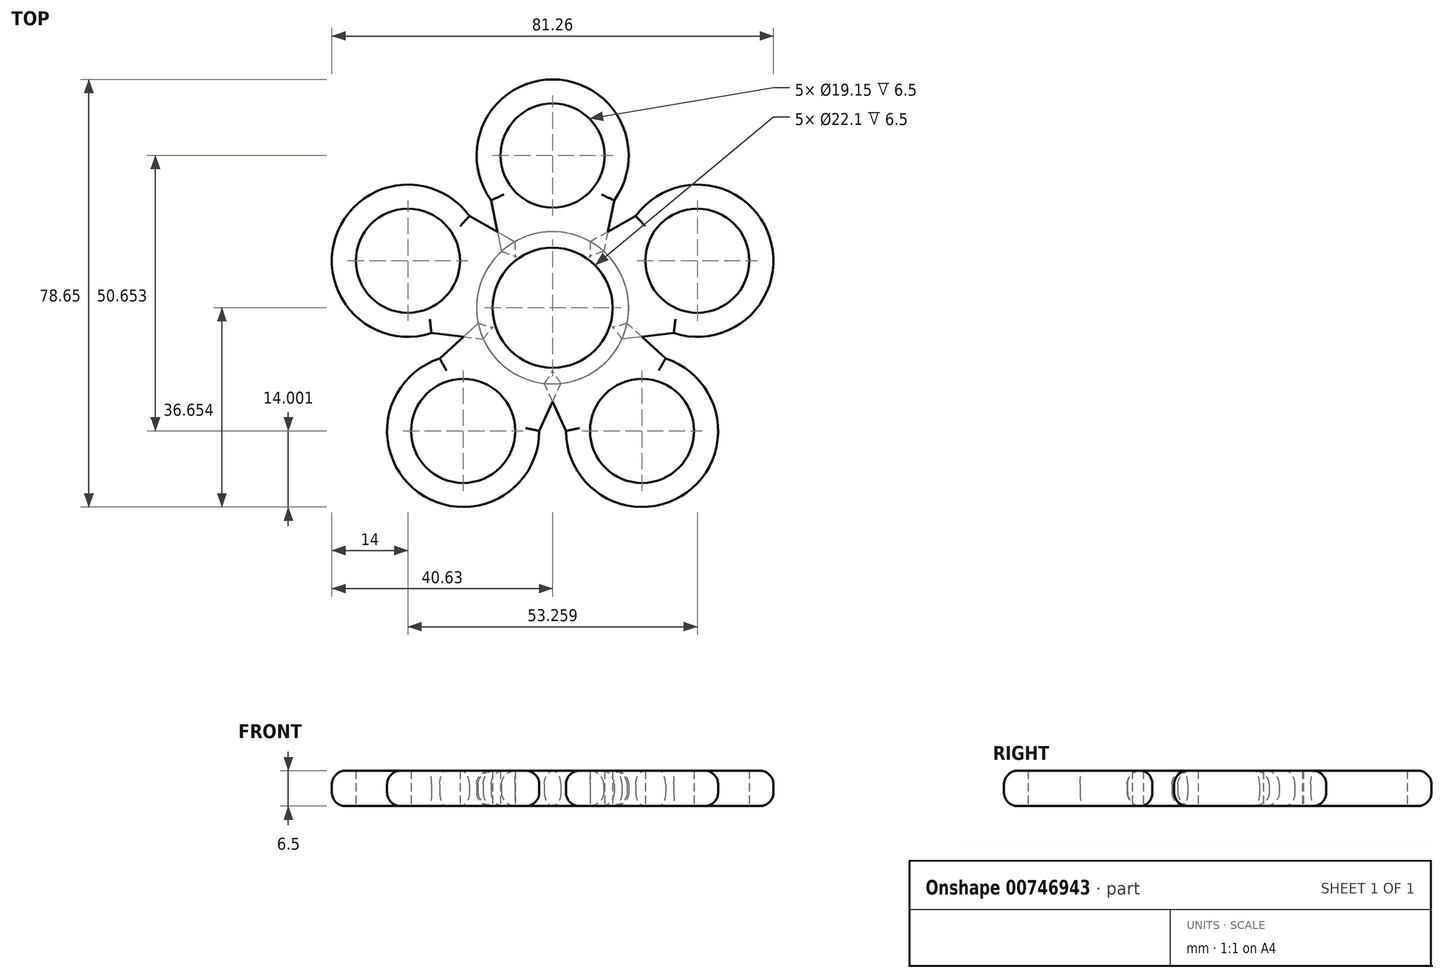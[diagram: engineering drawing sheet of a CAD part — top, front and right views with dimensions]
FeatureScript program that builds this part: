
annotation { "Feature Type Name" : "Feature", "Feature Type Description" : "" }
export const myFeature = defineFeature(function(context is Context, id is Id, definition is map)
    precondition{}
    {
        {
            var Q0;
            Q0=qCreatedBy(makeId("Top.planeOp"),FACE);
            var sketch = newSketch(context, id + "F0", { "sketchPlane" : qUnion([Q0])});
            skLineSegment(sketch, "E0.bottom", {"start": v(3.29, -10.32) * mm, "end": v(-3.29, -10.32) * mm});
            skLineSegment(sketch, "E0.top", {"start": v(13, 17.68) * mm, "end": v(-13, 17.68) * mm});
            skCircle(sketch, "E1", {"center": v(0, 17.68) * mm, "radius": 14 * mm});
            skCircle(sketch, "E2", {"center": v(0, 17.68) * mm, "radius": 9.57 * mm});
            skCircle(sketch, "E3", {"center": v(0, -10.32) * mm, "radius": 14 * mm});
            skCircle(sketch, "E4", {"center": v(0, -10.32) * mm, "radius": 11.05 * mm});
            skLineSegment(sketch, "E5", {"start": v(13, 17.68) * mm, "end": v(9.42, 0.04) * mm});
            skLineSegment(sketch, "E6", {"start": v(-13, 17.68) * mm, "end": v(-9.42, 0.04) * mm});
            skSolve(sketch);
        }
        {
            var Q0;
            {var subQ1=sQuery(id+"F0.wireOp",EDGE,"E0.top");var subQ8=sQuery(id+"F0.wireOp",EDGE,"E5");var subQ10=makeQuery(id+"F0.imprint","INTERSECT",VERTEX,{"derivedFrom":[subQ1,subQ8]});Q0=makeQuery(id+"F0.imprint","IMPRINT",FACE,{"disambiguationData":[TD([[makeQuery(id+"F0.imprint","IMPRINT",EDGE,{"disambiguationData":[TD([[subQ10,-1.0]])],"derivedFrom":subQ1}),-1.0]])]});}
            var Q1;
            {var subQ0=sQuery(id+"F0.wireOp",EDGE,"E5");var subQ6=sQuery(id+"F0.wireOp",EDGE,"E0.top");var subQ10=makeQuery(id+"F0.imprint","INTERSECT",VERTEX,{"derivedFrom":[subQ6,subQ0]});Q1=makeQuery(id+"F0.imprint","IMPRINT",FACE,{"disambiguationData":[TD([[makeQuery(id+"F0.imprint","IMPRINT",EDGE,{"disambiguationData":[TD([[subQ10,-1.0]])],"derivedFrom":subQ6}),1.0]])]});}
            var Q2;
            {var subQ0=sQuery(id+"F0.wireOp",EDGE,"E6");var subQ1=sQuery(id+"F0.wireOp",EDGE,"E1");var subQ2=makeQuery(id+"F0.imprint","INTERSECT",VERTEX,{"derivedFrom":[subQ1,subQ0]});Q2=makeQuery(id+"F0.imprint","IMPRINT",FACE,{"disambiguationData":[TD([[makeQuery(id+"F0.imprint","IMPRINT",EDGE,{"disambiguationData":[TD([[subQ2,-1.0]])],"derivedFrom":subQ1}),-1.0]])]});}
            var Q3;
            Q3=makeQuery(id+"F0.imprint","IMPRINT",FACE,{"disambiguationData":[TD([[makeQuery(id+"F0.imprint","IMPRINT",EDGE,{"derivedFrom":sQuery(id+"F0.wireOp",EDGE,"E4")}),-1.0]])]});
            var Q4;
            {var subQ0=sQuery(id+"F0.wireOp",EDGE,"E5");var subQ1=sQuery(id+"F0.wireOp",EDGE,"E1");var subQ2=makeQuery(id+"F0.imprint","INTERSECT",VERTEX,{"derivedFrom":[subQ1,subQ0]});Q4=makeQuery(id+"F0.imprint","IMPRINT",FACE,{"disambiguationData":[TD([[makeQuery(id+"F0.imprint","IMPRINT",EDGE,{"disambiguationData":[TD([[subQ2,1.0]])],"derivedFrom":subQ1}),-1.0]])]});}
            extrude(context, id + "F1", {"entities" : qUnion([Q0, Q1, Q2, Q3, Q4]), "depth" : 6.5 * mm, "offsetDistance" : 25 * mm});
        }
        {
            var Q0;
            Q0=makeQuery(id+"F1.opExtrude","CAP_EDGE",EDGE,{"disambiguationData":[OSD([sQuery(id+"F0.wireOp",EDGE,"E5")])],"isStart":false});
            var Q1;
            Q1=makeQuery(id+"F1.opExtrude","CAP_EDGE",EDGE,{"disambiguationData":[OSD([sQuery(id+"F0.wireOp",EDGE,"E1")])],"isStart":false});
            var Q2;
            Q2=makeQuery(id+"F1.opExtrude","CAP_EDGE",EDGE,{"disambiguationData":[OSD([sQuery(id+"F0.wireOp",EDGE,"E6")])],"isStart":false});
            var Q3;
            Q3=makeQuery(id+"F1.opExtrude","CAP_EDGE",EDGE,{"disambiguationData":[OSD([sQuery(id+"F0.wireOp",EDGE,"E3")])],"isStart":false});
            var Q4;
            Q4=makeQuery(id+"F1.opExtrude","CAP_EDGE",EDGE,{"disambiguationData":[OSD([sQuery(id+"F0.wireOp",EDGE,"E5")])],"isStart":true});
            var Q5;
            Q5=makeQuery(id+"F1.opExtrude","CAP_EDGE",EDGE,{"disambiguationData":[OSD([sQuery(id+"F0.wireOp",EDGE,"E1")])],"isStart":true});
            var Q6;
            Q6=makeQuery(id+"F1.opExtrude","CAP_EDGE",EDGE,{"disambiguationData":[OSD([sQuery(id+"F0.wireOp",EDGE,"E6")])],"isStart":true});
            var Q7;
            Q7=makeQuery(id+"F1.opExtrude","CAP_EDGE",EDGE,{"disambiguationData":[OSD([sQuery(id+"F0.wireOp",EDGE,"E3")])],"isStart":true});
            fillet(context, id + "F2", {"entities" : qUnion([Q0, Q1, Q2, Q3, Q4, Q5, Q6, Q7]), "radius" : 2.5 * mm, "tangentPropagation" : true, "allowEdgeOverflow" : false});
        }
        {
            var Q0;
            Q0=makeQuery(id+"F1.opExtrude","SWEPT_BODY",BODY,{"disambiguationData":[OSD([sQuery(id+"F0.wireOp",EDGE,"E1"),sQuery(id+"F0.wireOp",EDGE,"E2"),sQuery(id+"F0.wireOp",EDGE,"E3"),sQuery(id+"F0.wireOp",EDGE,"E4"),sQuery(id+"F0.wireOp",EDGE,"E5"),sQuery(id+"F0.wireOp",EDGE,"E6")])]});
            var Q1;
            Q1=sQuery(id+"F0.wireOp",EDGE,"E3");
            circularPattern(context, id + "F3", {"entities" : qUnion([Q0]), "axis" : qUnion([Q1]), "angle" : 360 * degree, "instanceCount" : 5, "equalSpace" : true});
        }
    });
